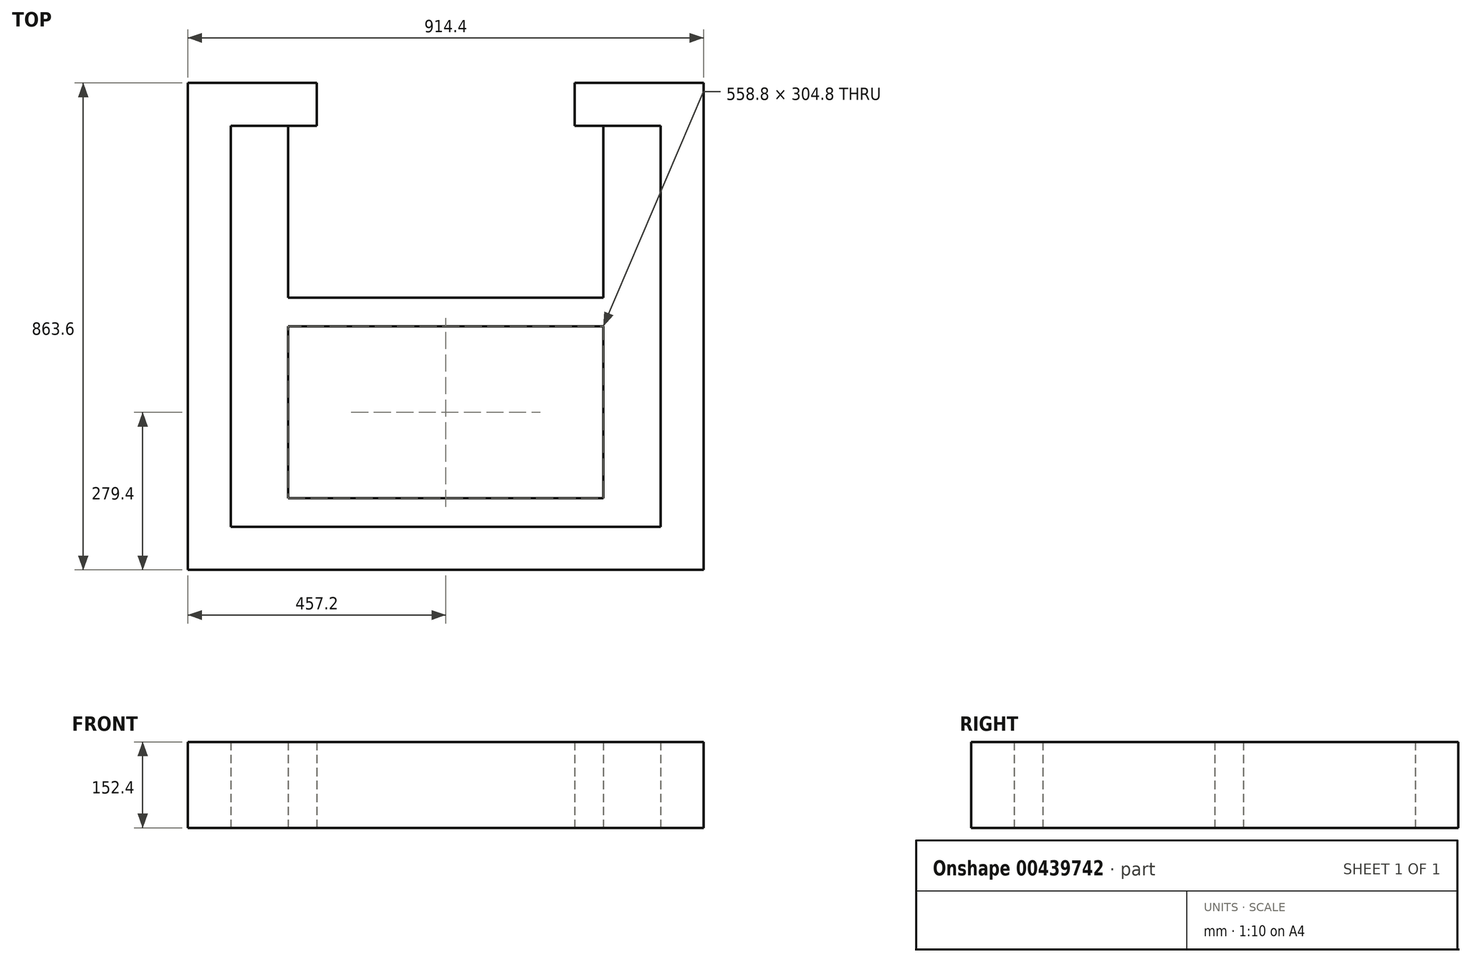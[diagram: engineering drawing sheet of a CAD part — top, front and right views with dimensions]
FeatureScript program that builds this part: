
annotation { "Feature Type Name" : "Feature", "Feature Type Description" : "" }
export const myFeature = defineFeature(function(context is Context, id is Id, definition is map)
    precondition{}
    {
        {
            var Q0;
            Q0=qCreatedBy(makeId("Top.planeOp"),FACE);
            var sketch = newSketch(context, id + "F0", { "sketchPlane" : qUnion([Q0])});
            skLineSegment(sketch, "E0.bottom", {"start": v(381, 355.6) * mm, "end": v(228.6, 355.6) * mm});
            skLineSegment(sketch, "E0.top", {"start": v(381, -355.6) * mm, "end": v(-381, -355.6) * mm});
            skLineSegment(sketch, "E0.left", {"start": v(381, 355.6) * mm, "end": v(381, -355.6) * mm});
            skLineSegment(sketch, "E0.right", {"start": v(-381, 355.6) * mm, "end": v(-381, -355.6) * mm});
            skPoint(sketch, "E0.middle", {"position": v(0, 0) * mm});
            skLineSegment(sketch, "E1.bottom", {"start": v(-457.2, 431.8) * mm, "end": v(-228.6, 431.8) * mm});
            skLineSegment(sketch, "E1.top", {"start": v(-457.2, -431.8) * mm, "end": v(457.2, -431.8) * mm});
            skLineSegment(sketch, "E1.left", {"start": v(-457.2, 431.8) * mm, "end": v(-457.2, -431.8) * mm});
            skLineSegment(sketch, "E1.right", {"start": v(457.2, 431.8) * mm, "end": v(457.2, -431.8) * mm});
            skLineSegment(sketch, "E2", {"start": v(-228.6, 431.8) * mm, "end": v(-228.6, 355.6) * mm});
            skLineSegment(sketch, "E3", {"start": v(228.6, 355.6) * mm, "end": v(228.6, 431.8) * mm});
            skLineSegment(sketch, "E4.trimOffspring", {"start": v(228.6, 431.8) * mm, "end": v(457.2, 431.8) * mm});
            skLineSegment(sketch, "E5.trimOffspring", {"start": v(-228.6, 355.6) * mm, "end": v(-381, 355.6) * mm});
            skSolve(sketch);
        }
        {
            var Q0;
            Q0=qCreatedBy(makeId("Top.planeOp"),FACE);
            var sketch = newSketch(context, id + "F1", { "sketchPlane" : qUnion([Q0])});
            skLineSegment(sketch, "E6.bottom", {"start": v(-381, 355.6) * mm, "end": v(-279.4, 355.6) * mm});
            skLineSegment(sketch, "E6.top", {"start": v(-381, -355.6) * mm, "end": v(-279.4, -355.6) * mm});
            skLineSegment(sketch, "E6.left", {"start": v(-381, 355.6) * mm, "end": v(-381, -355.6) * mm});
            skLineSegment(sketch, "E6.right", {"start": v(-279.4, 355.6) * mm, "end": v(-279.4, 50.8) * mm});
            skLineSegment(sketch, "E7.bottom", {"start": v(381, -355.6) * mm, "end": v(279.4, -355.6) * mm});
            skLineSegment(sketch, "E7.top", {"start": v(381, 355.6) * mm, "end": v(279.4, 355.6) * mm});
            skLineSegment(sketch, "E7.left", {"start": v(381, 355.6) * mm, "end": v(381, -355.6) * mm});
            skLineSegment(sketch, "E7.right", {"start": v(279.4, 0) * mm, "end": v(279.4, -304.8) * mm});
            skLineSegment(sketch, "E8", {"start": v(-279.4, -355.6) * mm, "end": v(279.4, -355.6) * mm});
            skLineSegment(sketch, "E9", {"start": v(-279.4, -304.8) * mm, "end": v(279.4, -304.8) * mm});
            skLineSegment(sketch, "E10", {"start": v(-279.4, 50.8) * mm, "end": v(279.4, 50.8) * mm});
            skLineSegment(sketch, "E11", {"start": v(-279.4, 0) * mm, "end": v(279.4, 0) * mm});
            skLineSegment(sketch, "E12.trimOffspring", {"start": v(-279.4, 0) * mm, "end": v(-279.4, -304.8) * mm});
            skLineSegment(sketch, "E13.trimOffspring", {"start": v(279.4, 355.6) * mm, "end": v(279.4, 50.8) * mm});
            skSolve(sketch);
        }
        {
            var Q0;
            Q0=makeQuery(id+"F0.imprint","IMPRINT",FACE,{"disambiguationData":[TD([[makeQuery(id+"F0.imprint","IMPRINT",EDGE,{"derivedFrom":sQuery(id+"F0.wireOp",EDGE,"E0.bottom")}),-1.0]])]});
            extrude(context, id + "F2", {"entities" : qUnion([Q0]), "depth" : 152.4 * mm});
        }
        {
            var Q0;
            Q0=makeQuery(id+"F1.imprint","IMPRINT",FACE,{"disambiguationData":[TD([[makeQuery(id+"F1.imprint","IMPRINT",EDGE,{"derivedFrom":sQuery(id+"F1.wireOp",EDGE,"E6.bottom")}),-1.0]])]});
            extrude(context, id + "F3", {"entities" : qUnion([Q0]), "depth" : 152.4 * mm});
        }
    });
